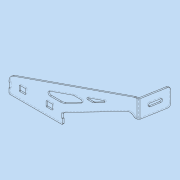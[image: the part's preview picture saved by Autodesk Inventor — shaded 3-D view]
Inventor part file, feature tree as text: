
AUTODESK INVENTOR PART (.ipt)
format: ipt  version: 2020 (Build 240168000, 168)  size: 424,960 bytes
history: native  units: mm
features: other x3, extrude x1, plane x1
ambient origin geometry x8: Origin, YZ Plane, XZ Plane, XY Plane, X Axis, Y Axis, Z Axis, Center Point
bodies: Body1 (feature_tree)
feature tree (5):
  other  "實體1"
  extrude  "擠出1"  Depth=130.0mm
  other  "折彎零件1"
  plane  "工作平面1"
  other  "定義1"
